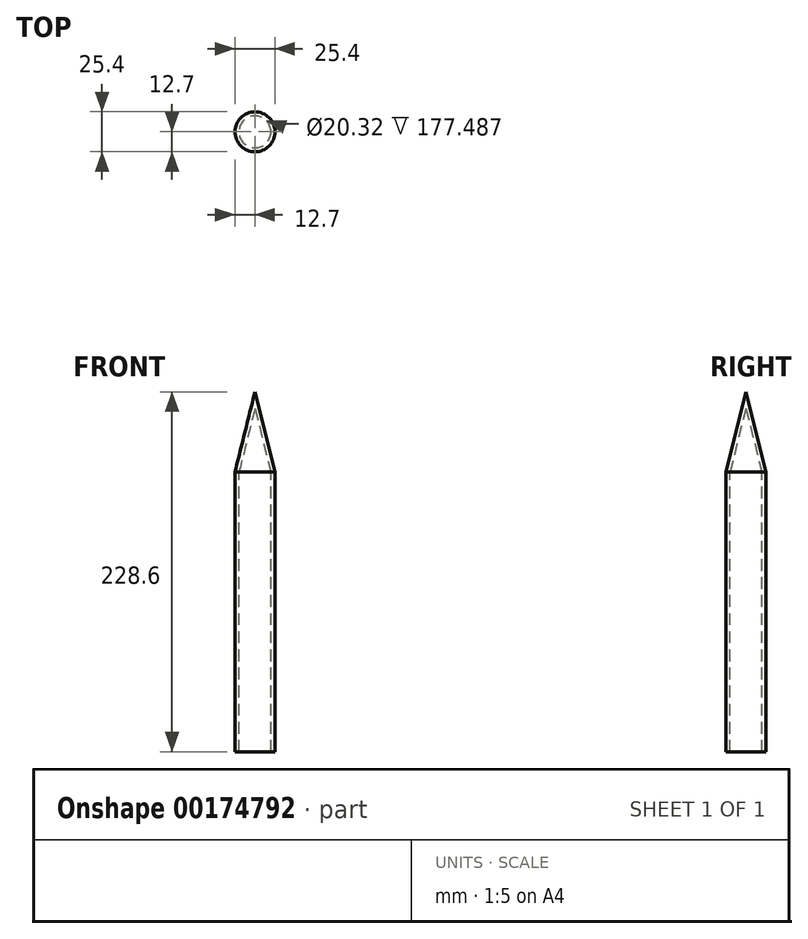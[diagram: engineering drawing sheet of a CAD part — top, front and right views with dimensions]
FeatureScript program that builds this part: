
annotation { "Feature Type Name" : "Feature", "Feature Type Description" : "" }
export const myFeature = defineFeature(function(context is Context, id is Id, definition is map)
    precondition{}
    {
        {
            var Q0;
            Q0=qCreatedBy(makeId("Front.planeOp"),FACE);
            var sketch = newSketch(context, id + "F0", { "sketchPlane" : qUnion([Q0])});
            skLineSegment(sketch, "E0", {"start": v(0, 62.26) * mm, "end": v(0, -115.54) * mm});
            skLineSegment(sketch, "E1", {"start": v(0, 62.26) * mm, "end": v(12.7, 62.26) * mm});
            skLineSegment(sketch, "E2", {"start": v(12.7, 62.26) * mm, "end": v(12.7, -115.54) * mm});
            skLineSegment(sketch, "E3", {"start": v(12.7, -115.54) * mm, "end": v(0, -115.54) * mm});
            skLineSegment(sketch, "E4", {"start": v(0, 62.26) * mm, "end": v(0, 113.06) * mm});
            skLineSegment(sketch, "E5", {"start": v(0, 113.06) * mm, "end": v(12.7, 62.26) * mm});
            skSolve(sketch);
        }
        {
            var Q0;
            Q0=makeQuery(id+"F0.imprint","IMPRINT",FACE,{"disambiguationData":[TD([[makeQuery(id+"F0.imprint","IMPRINT",EDGE,{"derivedFrom":sQuery(id+"F0.wireOp",EDGE,"E0")}),1.0]])]});
            var Q1;
            Q1=makeQuery(id+"F0.imprint","IMPRINT",FACE,{"disambiguationData":[TD([[makeQuery(id+"F0.imprint","IMPRINT",EDGE,{"derivedFrom":sQuery(id+"F0.wireOp",EDGE,"E1")}),1.0]])]});
            var Q2;
            Q2=sQuery(id+"F0.wireOp",EDGE,"E0");
            revolve(context, id + "F1", {"entities" : qUnion([Q0, Q1]), "axis" : qUnion([Q2]), "revolveType" : RevolveType.FULL});
        }
        {
            var Q0;
            Q0=makeQuery(id+"F1.opRevolve","SWEPT_FACE",FACE,{"disambiguationData":[OSD([sQuery(id+"F0.wireOp",EDGE,"E1")])]});
            var Q1;
            Q1=makeQuery(id+"F1.opRevolve","SWEPT_FACE",FACE,{"disambiguationData":[OSD([sQuery(id+"F0.wireOp",EDGE,"E3")])]});
            shell(context, id + "F2", {"entities" : qUnion([Q0, Q1]), "thickness" : 2.54 * mm});
        }
    });
